# Revit family: СИБИТ_Узел_Перемычка_Высота 300 мм_D600(D700) B3,5
name_source: partatom
category: Обобщенные модели
revit_build: Autodesk Revit 2017 (Build: 20171027_0315(x64)
units: mm (PartAtom-declared; Revit-internal decimal feet)

## family parameters
Всегда вертикально = Да
Заголовок OmniClass = Beams
Может служить основой для арматурных стержней = Нет
Номер OmniClass = 23.25.30.11.14.14
Общий = Да
Основа = Стена
При загрузке вырезать с полостями = Да
Размер круглого соединителя = Использовать диаметр
Тип детали = Нормальный
Точка расчета площади = Нет

## types (2) — shared parameters
Bimon = www.bimon.ru
IFC Classification = Beam
Omniclass Code = 23.25.30.11.14.14
Omniclass Title = Beams
UNSPSC Code = 30101700
UNSPSC Title = Beams
URL = www.sibyt.ru
Uniclass 2015 Code = EF_20_20
Uniclass 2015 Title = Beams
Изготовитель = СИБИТ
Ключевая пометка = 04200.B2
Контактный телефон = +7 (383) 363-90-90
Разработчик модели = Bimon - сервисный провайдер услуг информационного моделирования

## per-type parameters (varying)
| type | Материал несущих конструкций | Сертификат соответствия | Типоразмер_перемычки |
| СИБИТ_Узел_Перемычка 300 мм_D700 B3,5 | СИБИТ_Перемычки_Газобетон D700 B3,5 |  | 2 |
| СИБИТ_Узел_Перемычка 300 мм_D600 B3,5 | СИБИТ_Перемычки_Газобетон D600 B3,5 | https://sibyt.ru | 1 |
